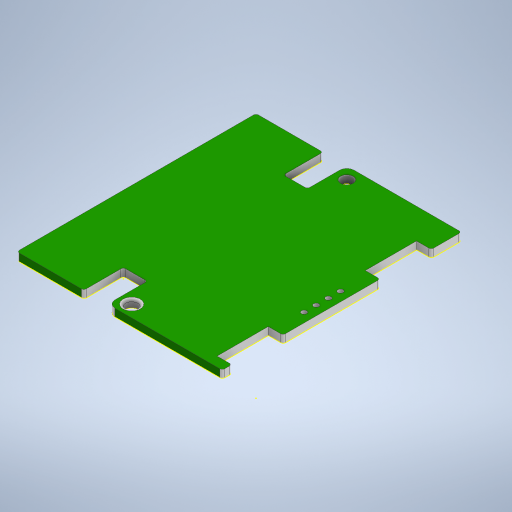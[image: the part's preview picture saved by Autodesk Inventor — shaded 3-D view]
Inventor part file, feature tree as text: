
AUTODESK INVENTOR PART (.ipt)
format: ipt  version: 2023 (Build 270158000, 158)  size: 443,392 bytes
history: native  units: mm
features: other x10, sketch x10, reference x9, extrude x8, projected_geometry x6, fillet x5, hole x1
ambient origin geometry x8: Origin, YZ Plane, XZ Plane, XY Plane, X Axis, Y Axis, Z Axis, Center Point
bodies: Body1 (feature_tree)
feature tree (49):
  other  "Bryła1"
  extrude  "Wyciągnięcie proste1"  Depth=50.0mm
  extrude  "Wyciągnięcie proste2"  Depth=50.0mm
  extrude  "Wyciągnięcie proste3"  Depth=1.6mm TaperAngle=0.0deg
  extrude  "Wyciągnięcie proste4"  TaperAngle=0.0deg  [1 undecoded]
  extrude  "Wyciągnięcie proste5"  Depth=2.3mm
  fillet  "Zaokrąglenie2"  Radius=2.3mm
  extrude  "Wyciągnięcie proste7"  TaperAngle=0.0deg  [1 undecoded]
  extrude  "Wyciągnięcie proste8"  Depth=1.1mm
  fillet  "Zaokrąglenie3"  Radius=10.0mm
  extrude  "Wyciągnięcie proste10"  Depth=6.34mm
  fillet  "Zaokrąglenie4"  [1 undecoded]
  fillet  "Zaokrąglenie5"  Radius=2.0mm
  hole  "Otwór2"  [1 undecoded]
  fillet  "Zaokrąglenie6"  [1 undecoded]
  sketch  "Szkic14"
  sketch  "Szkic1"
  sketch  "Szkic2"
  projected_geometry  "Pętla rzutowana1"
  reference  "Odniesienie1"
  sketch  "Szkic3"
  reference  "Odniesienie2"
  reference  "Odniesienie3"
  sketch  "Szkic4"
  sketch  "Szkic5"
  projected_geometry  "Pętla rzutowana2"
  reference  "Odniesienie4"
  reference  "Odniesienie5"
  reference  "Odniesienie6"
  reference  "Odniesienie7"
  sketch  "Szkic7"
  projected_geometry  "Pętla rzutowana3"
  sketch  "Szkic9"
  projected_geometry  "Pętla rzutowana5"
  sketch  "Szkic11"
  projected_geometry  "Pętla rzutowana6"
  sketch  "Szkic13"
  reference  "Odniesienie12"
  reference  "Odniesienie13"
  projected_geometry  "Pętla rzutowana7"
  other  "<userpath>\Documents\Inventor\MikroNalesnik\byk_alternator.iam"
  other  "byk_alternator.iam"
  other  "noz2:1"
  other  "TOF_VL53L0X (1):1"
  other  "TOF_VL53L0X (1):2"
  other  "wach:1"
  other  "servo_mini_1370hd_cos:2"
  other  "kolko:2"
  other  "podstawa:1"
note: 5 required parameter values undecoded (feature->parameter linkage not recoverable at this tier; creation-order binding heuristic only, values carry confidence <= 0.55)
